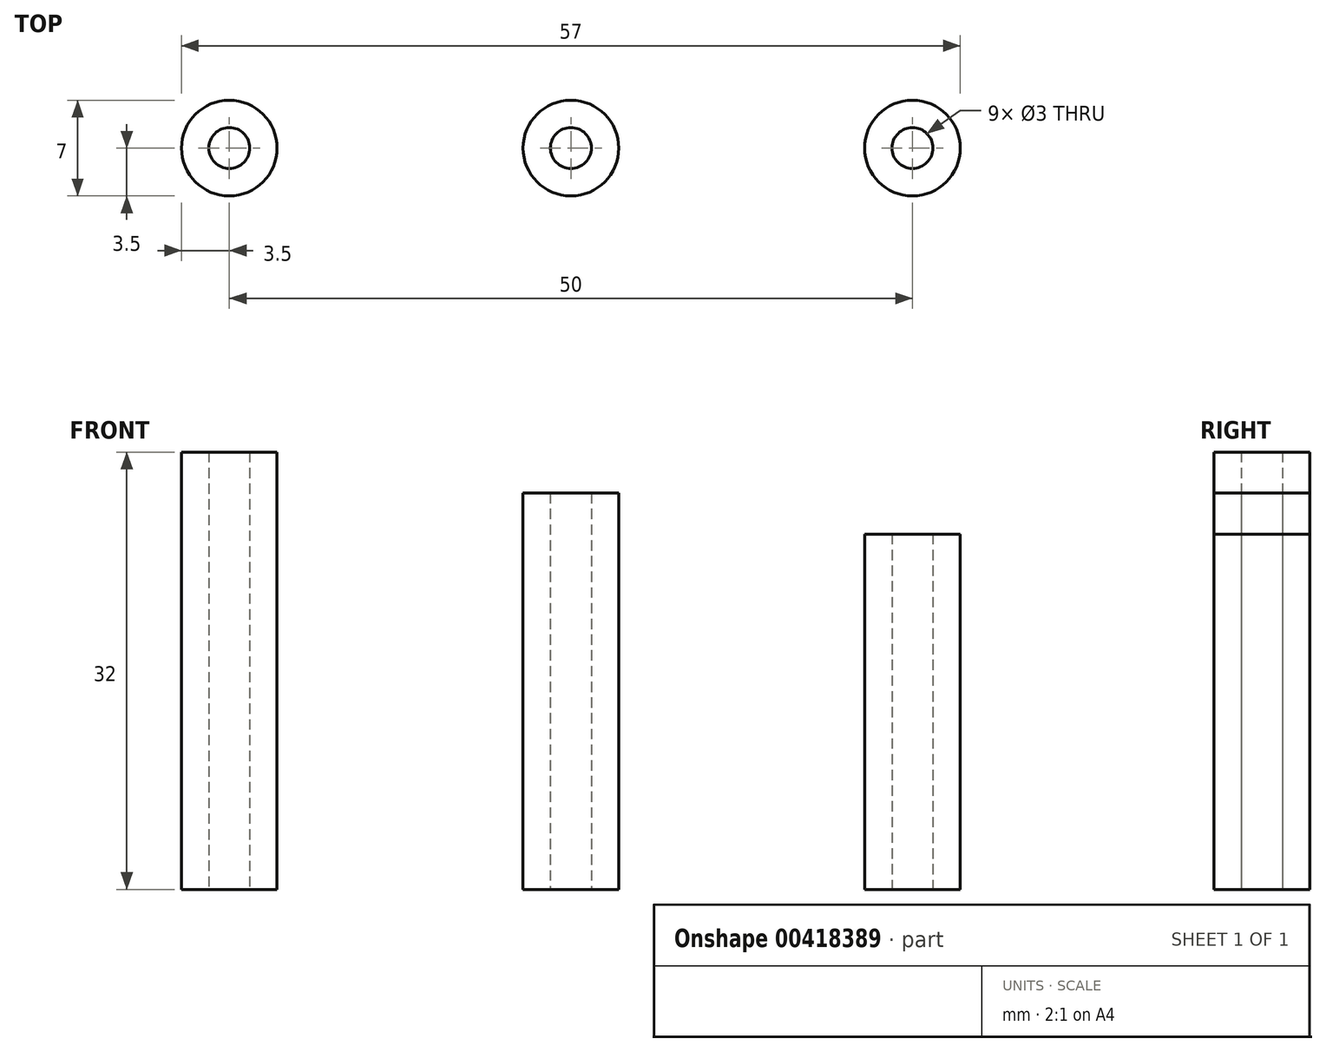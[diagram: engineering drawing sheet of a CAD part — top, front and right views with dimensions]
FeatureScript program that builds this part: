
annotation { "Feature Type Name" : "Feature", "Feature Type Description" : "" }
export const myFeature = defineFeature(function(context is Context, id is Id, definition is map)
    precondition{}
    {
        {
            var Q0;
            Q0=qCreatedBy(makeId("Top.planeOp"),FACE);
            var sketch = newSketch(context, id + "F0", { "sketchPlane" : qUnion([Q0])});
            skCircle(sketch, "E0", {"center": v(0, 0) * mm, "radius": 1.5 * mm});
            skCircle(sketch, "E1.1.0.0", {"center": v(25, 0) * mm, "radius": 1.5 * mm});
            skCircle(sketch, "E1.2.0.0", {"center": v(50, 0) * mm, "radius": 1.5 * mm});
            skLineSegment(sketch, "E1.direction1", {"start": v(0, 0) * mm, "end": v(25, 0) * mm, "construction": true});
            skCircle(sketch, "E2", {"center": v(0, 0) * mm, "radius": 3.5 * mm});
            skCircle(sketch, "E3.1.0.0", {"center": v(25, 0) * mm, "radius": 3.5 * mm});
            skCircle(sketch, "E3.2.0.0", {"center": v(50, 0) * mm, "radius": 3.5 * mm});
            skSolve(sketch);
        }
        {
            var Q0;
            Q0=makeQuery(id+"F0.imprint","IMPRINT",FACE,{"disambiguationData":[TD([[makeQuery(id+"F0.imprint","IMPRINT",EDGE,{"derivedFrom":sQuery(id+"F0.wireOp",EDGE,"E0")}),-1.0]])]});
            extrude(context, id + "F1", {"entities" : qUnion([Q0]), "depth" : 32 * mm});
        }
        {
            var Q0;
            Q0=makeQuery(id+"F0.imprint","IMPRINT",FACE,{"disambiguationData":[TD([[makeQuery(id+"F0.imprint","IMPRINT",EDGE,{"derivedFrom":sQuery(id+"F0.wireOp",EDGE,"E1.1.0.0")}),-1.0]])]});
            extrude(context, id + "F2", {"entities" : qUnion([Q0]), "depth" : 29 * mm});
        }
        {
            var Q0;
            Q0=makeQuery(id+"F0.imprint","IMPRINT",FACE,{"disambiguationData":[TD([[makeQuery(id+"F0.imprint","IMPRINT",EDGE,{"derivedFrom":sQuery(id+"F0.wireOp",EDGE,"E1.2.0.0")}),-1.0]])]});
            extrude(context, id + "F3", {"entities" : qUnion([Q0]), "depth" : 26 * mm});
        }
    });
